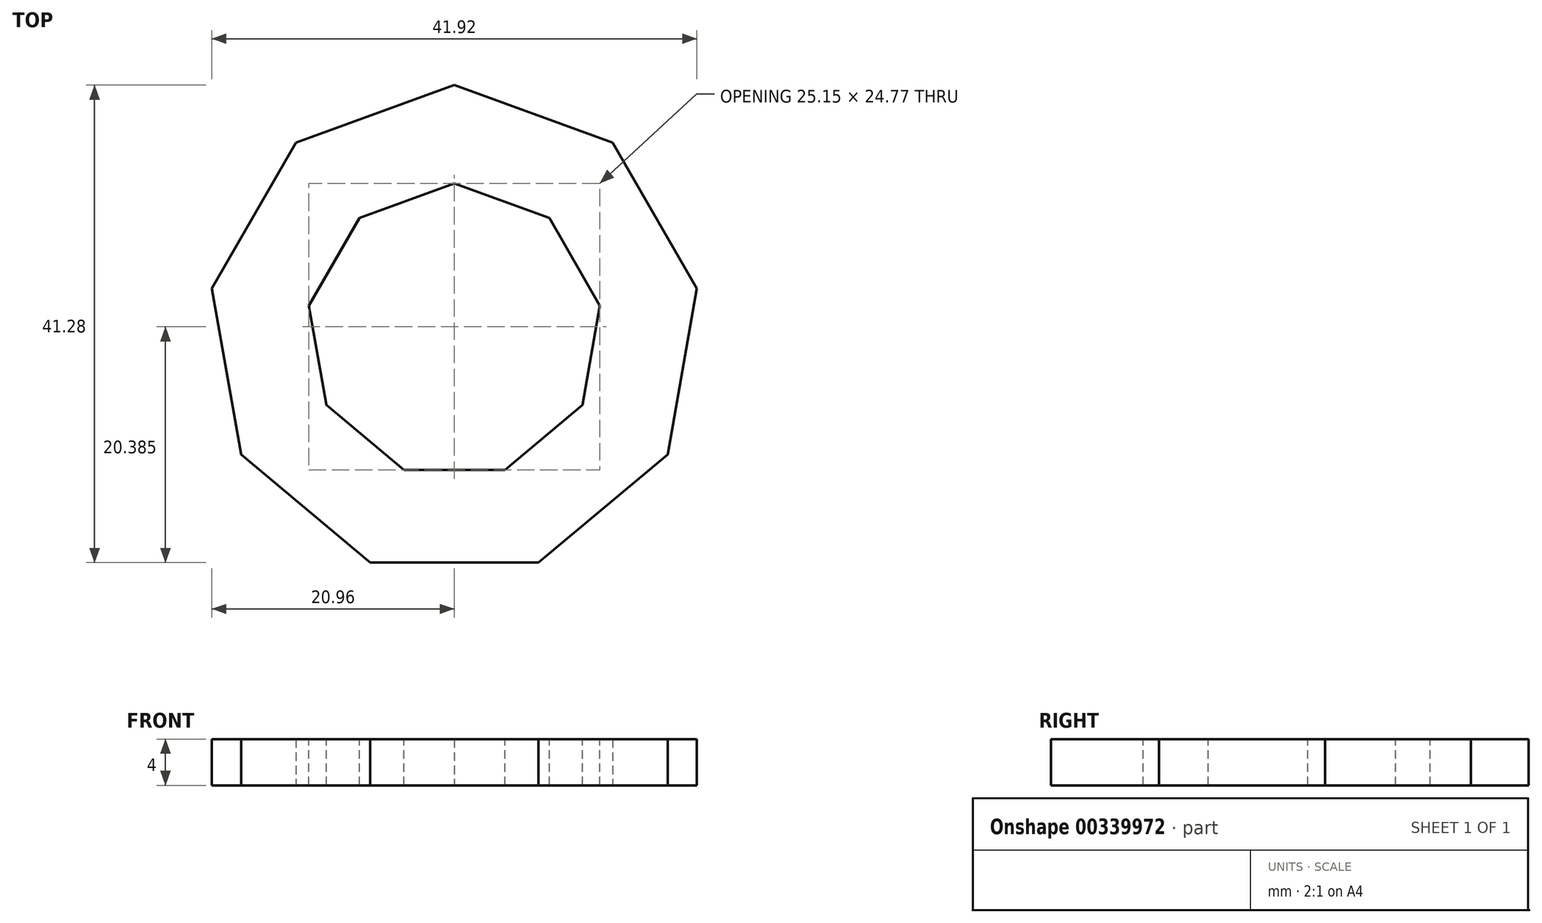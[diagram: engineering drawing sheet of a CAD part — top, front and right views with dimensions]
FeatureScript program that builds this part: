
annotation { "Feature Type Name" : "Feature", "Feature Type Description" : "" }
export const myFeature = defineFeature(function(context is Context, id is Id, definition is map)
    precondition{}
    {
        {
            var Q0;
            Q0=qCreatedBy(makeId("Top.planeOp"),FACE);
            var sketch = newSketch(context, id + "F0", { "sketchPlane" : qUnion([Q0])});
            skCircle(sketch, "E0.cCircle", {"center": v(0, 0) * mm, "radius": 20 * mm, "construction": true});
            skLineSegment(sketch, "E0.0", {"start": v(7.28, -20) * mm, "end": v(-7.28, -20) * mm});
            skLineSegment(sketch, "E0.1", {"start": v(-7.28, -20) * mm, "end": v(-18.43, -10.64) * mm});
            skLineSegment(sketch, "E0.2", {"start": v(-18.43, -10.64) * mm, "end": v(-20.96, 3.7) * mm});
            skLineSegment(sketch, "E0.3", {"start": v(-20.96, 3.7) * mm, "end": v(-13.68, 16.3) * mm});
            skLineSegment(sketch, "E0.4", {"start": v(-13.68, 16.3) * mm, "end": v(0, 21.28) * mm});
            skLineSegment(sketch, "E0.5", {"start": v(0, 21.28) * mm, "end": v(13.68, 16.3) * mm});
            skLineSegment(sketch, "E0.6", {"start": v(13.68, 16.3) * mm, "end": v(20.96, 3.7) * mm});
            skLineSegment(sketch, "E0.7", {"start": v(20.96, 3.7) * mm, "end": v(18.43, -10.64) * mm});
            skLineSegment(sketch, "E0.8", {"start": v(18.43, -10.64) * mm, "end": v(7.28, -20) * mm});
            skPoint(sketch, "E0.0.midPoint", {"position": v(0, -20) * mm});
            skSolve(sketch);
        }
        {
            var Q0;
            Q0 = qSketchRegion(id + "F0", true);
            extrude(context, id + "F1", {"entities" : qUnion([Q0]), "depth" : 4 * mm, "offsetDistance" : 25 * mm});
        }
        {
            var Q0;
            Q0=makeQuery(id+"F1.opExtrude","CAP_FACE",FACE,{"disambiguationData":[OSD([sQuery(id+"F0.wireOp",EDGE,"E0.0"),sQuery(id+"F0.wireOp",EDGE,"E0.1"),sQuery(id+"F0.wireOp",EDGE,"E0.2"),sQuery(id+"F0.wireOp",EDGE,"E0.3"),sQuery(id+"F0.wireOp",EDGE,"E0.4"),sQuery(id+"F0.wireOp",EDGE,"E0.5"),sQuery(id+"F0.wireOp",EDGE,"E0.6"),sQuery(id+"F0.wireOp",EDGE,"E0.7"),sQuery(id+"F0.wireOp",EDGE,"E0.8")])],"isStart":false});
            var sketch = newSketch(context, id + "F2", { "sketchPlane" : qUnion([Q0])});
            skLineSegment(sketch, "E1.0", {"start": v(-4.37, -12) * mm, "end": v(4.37, -12) * mm});
            skLineSegment(sketch, "E1.1", {"start": v(-11.06, -6.39) * mm, "end": v(-4.37, -12) * mm});
            skLineSegment(sketch, "E1.2", {"start": v(4.37, -12) * mm, "end": v(11.06, -6.39) * mm});
            skLineSegment(sketch, "E1.3", {"start": v(-12.58, 2.22) * mm, "end": v(-11.06, -6.39) * mm});
            skLineSegment(sketch, "E1.4", {"start": v(-8.2, 9.78) * mm, "end": v(-12.58, 2.22) * mm});
            skLineSegment(sketch, "E1.5", {"start": v(11.06, -6.39) * mm, "end": v(12.58, 2.22) * mm});
            skLineSegment(sketch, "E1.6", {"start": v(12.58, 2.22) * mm, "end": v(8.2, 9.78) * mm});
            skLineSegment(sketch, "E1.7", {"start": v(8.2, 9.78) * mm, "end": v(0, 12.77) * mm});
            skLineSegment(sketch, "E1.8", {"start": v(0, 12.77) * mm, "end": v(-8.2, 9.78) * mm});
            skSolve(sketch);
        }
        {
            var Q0;
            Q0 = qSketchRegion(id + "F2", true);
            extrude(context, id + "F3", {"entities" : qUnion([Q0]), "operationType" : NewBodyOperationType.REMOVE, "oppositeDirection" : true, "depth" : 25 * mm, "offsetDistance" : 25 * mm});
        }
    });
